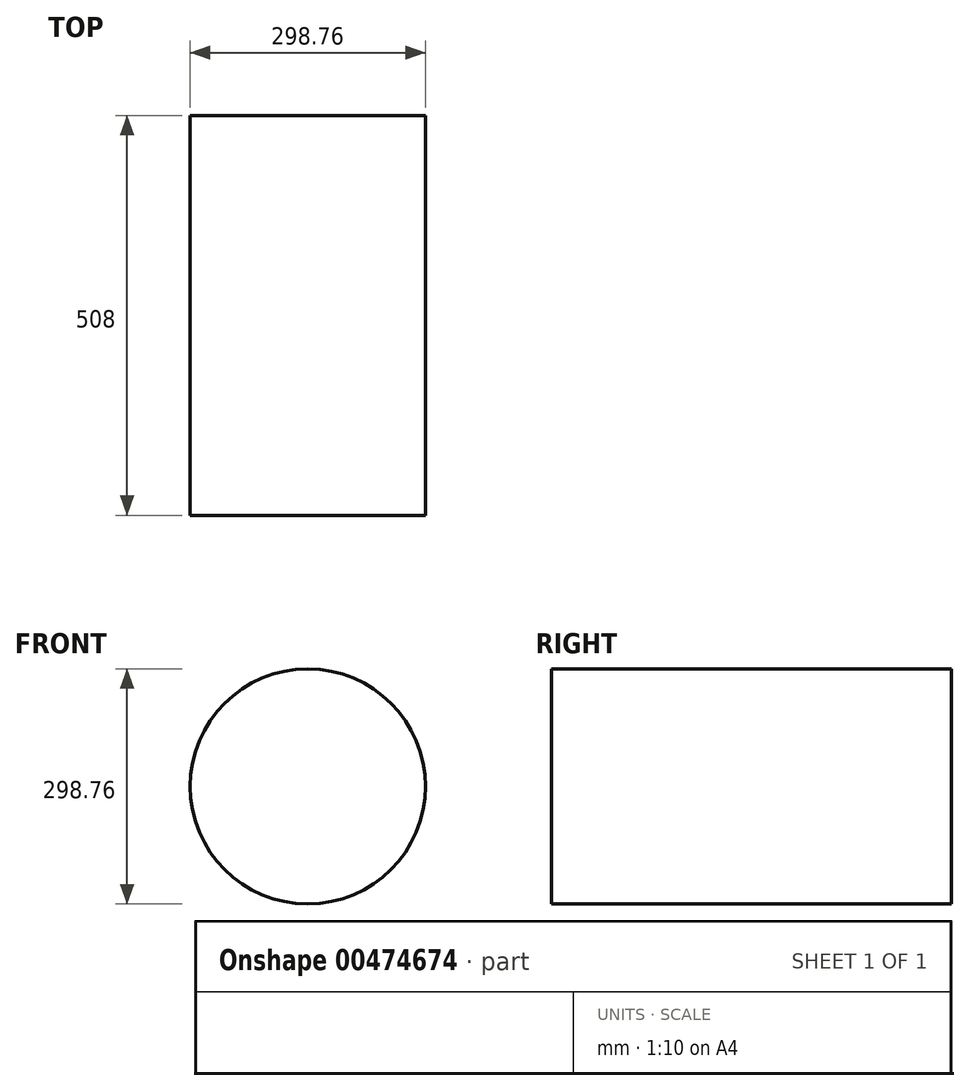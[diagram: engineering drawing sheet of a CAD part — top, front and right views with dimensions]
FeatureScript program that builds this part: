
annotation { "Feature Type Name" : "Feature", "Feature Type Description" : "" }
export const myFeature = defineFeature(function(context is Context, id is Id, definition is map)
    precondition{}
    {
        {
            var Q0;
            Q0=qCreatedBy(makeId("Front.planeOp"),FACE);
            var sketch = newSketch(context, id + "F0", { "sketchPlane" : qUnion([Q0])});
            skCircle(sketch, "E0", {"center": v(0, 0) * mm, "radius": 149.38 * mm});
            skSolve(sketch);
        }
        {
            var Q0;
            Q0=sQuery(id+"F0.wireOp",EDGE,"E0");
            extrude(context, id + "F1", {"bodyType" : ToolBodyType.SURFACE, "surfaceEntities" : qUnion([Q0]), "depth" : 508 * mm});
        }
    });
